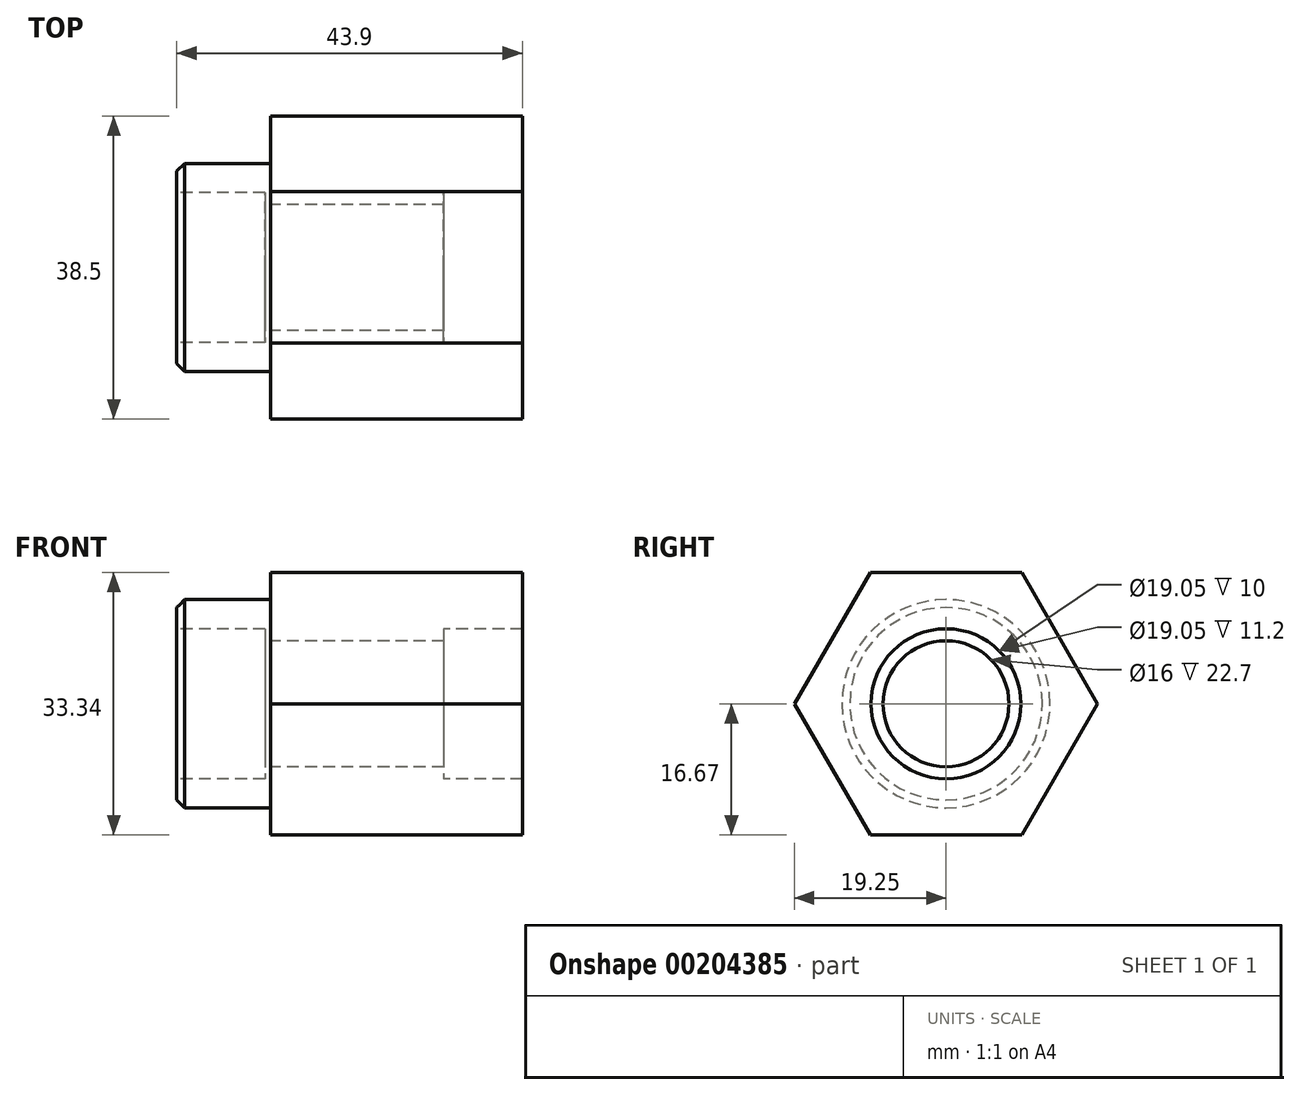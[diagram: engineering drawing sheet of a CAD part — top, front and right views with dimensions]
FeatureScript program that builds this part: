
annotation { "Feature Type Name" : "Feature", "Feature Type Description" : "" }
export const myFeature = defineFeature(function(context is Context, id is Id, definition is map)
    precondition{}
    {
        {
            var Q0;
            Q0=qCreatedBy(makeId("Front.planeOp"),FACE);
            var sketch = newSketch(context, id + "F0", { "sketchPlane" : qUnion([Q0])});
            skLineSegment(sketch, "E0", {"start": v(0, 0) * mm, "end": v(43.9, 0) * mm});
            skLineSegment(sketch, "E1", {"start": v(43.9, 9.53) * mm, "end": v(33.9, 9.52) * mm});
            skLineSegment(sketch, "E2", {"start": v(33.9, 9.52) * mm, "end": v(33.9, 8) * mm});
            skLineSegment(sketch, "E3", {"start": v(33.9, 8) * mm, "end": v(11.2, 8) * mm});
            skLineSegment(sketch, "E4", {"start": v(11.2, 8) * mm, "end": v(11.2, 9.52) * mm});
            skLineSegment(sketch, "E5", {"start": v(11.2, 9.52) * mm, "end": v(0, 9.52) * mm});
            skLineSegment(sketch, "E6", {"start": v(0, 9.52) * mm, "end": v(0, 13.22) * mm});
            skLineSegment(sketch, "E7", {"start": v(0, 13.22) * mm, "end": v(11.9, 13.22) * mm});
            skLineSegment(sketch, "E8", {"start": v(11.9, 13.22) * mm, "end": v(11.9, 20) * mm});
            skLineSegment(sketch, "E9", {"start": v(11.9, 20) * mm, "end": v(43.9, 20) * mm});
            skLineSegment(sketch, "E10", {"start": v(43.9, 20) * mm, "end": v(43.9, 9.53) * mm});
            skSolve(sketch);
        }
        {
            var Q0;
            Q0=makeQuery(id+"F0.imprint","IMPRINT",FACE,{"disambiguationData":[TD([[makeQuery(id+"F0.imprint","IMPRINT",EDGE,{"derivedFrom":sQuery(id+"F0.wireOp",EDGE,"E1")}),-1.0]])]});
            var Q1;
            Q1=sQuery(id+"F0.wireOp",EDGE,"E0");
            revolve(context, id + "F1", {"entities" : qUnion([Q0]), "axis" : qUnion([Q1]), "revolveType" : RevolveType.FULL});
        }
        {
            var Q0;
            Q0=makeQuery(id+"F1.opRevolve","SWEPT_FACE",FACE,{"disambiguationData":[OSD([sQuery(id+"F0.wireOp",EDGE,"E10")])]});
            var sketch = newSketch(context, id + "F2", { "sketchPlane" : qUnion([Q0])});
            skCircle(sketch, "E11.cCircle", {"center": v(0, 0) * mm, "radius": 19.25 * mm, "construction": true});
            skLineSegment(sketch, "E11.0", {"start": v(9.62, 16.67) * mm, "end": v(19.25, 0) * mm});
            skLineSegment(sketch, "E11.1", {"start": v(19.25, 0) * mm, "end": v(9.62, -16.67) * mm});
            skLineSegment(sketch, "E11.2", {"start": v(9.62, -16.67) * mm, "end": v(-9.62, -16.67) * mm});
            skLineSegment(sketch, "E11.3", {"start": v(-9.62, -16.67) * mm, "end": v(-19.25, 0) * mm});
            skLineSegment(sketch, "E11.4", {"start": v(-19.25, 0) * mm, "end": v(-9.62, 16.67) * mm});
            skLineSegment(sketch, "E11.5", {"start": v(-9.62, 16.67) * mm, "end": v(9.62, 16.67) * mm});
            skCircle(sketch, "E12", {"center": v(0, 0) * mm, "radius": 20 * mm});
            skSolve(sketch);
        }
        {
            var Q0;
            Q0 = qSketchRegion(id + "F2", true);
            extrude(context, id + "F3", {"entities" : qUnion([Q0]), "operationType" : NewBodyOperationType.REMOVE, "endBound" : BoundingType.THROUGH_ALL, "oppositeDirection" : true, "depth" : 25 * mm});
        }
        {
            var Q0;
            Q0=makeQuery(id+"F1.opRevolve","SWEPT_EDGE",EDGE,{"disambiguationData":[OSD([sQuery(id+"F0.wireOp",EDGE,"E6"),sQuery(id+"F0.wireOp",EDGE,"E7")])]});
            chamfer(context, id + "F4", {"entities" : qUnion([Q0]), "width" : 1 * mm, "tangentPropagation" : true});
        }
    });
